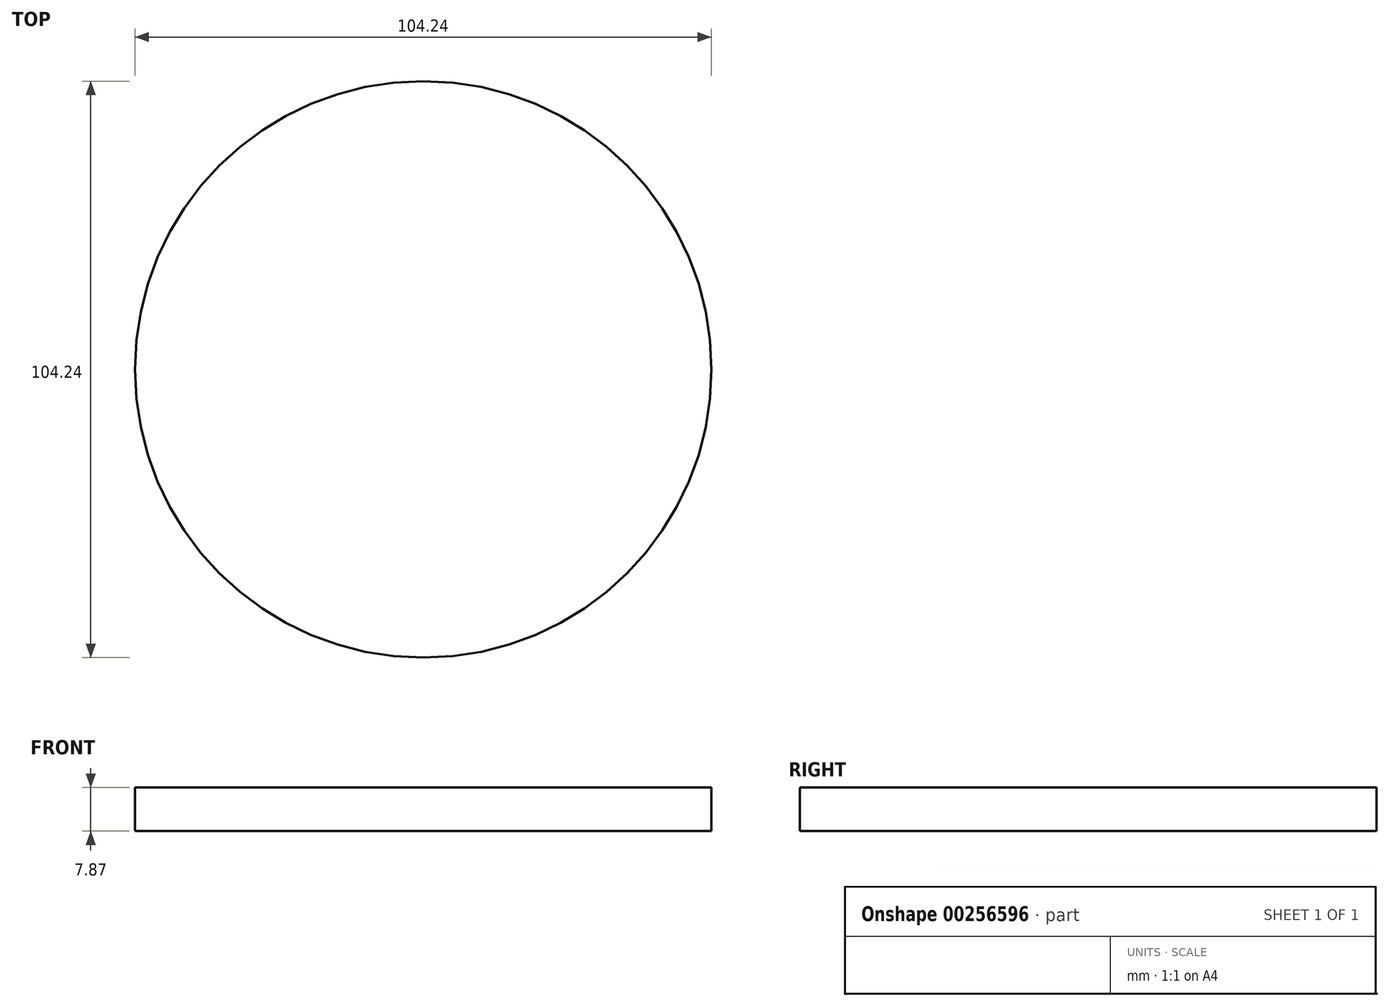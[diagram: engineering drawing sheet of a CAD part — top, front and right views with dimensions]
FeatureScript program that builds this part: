
annotation { "Feature Type Name" : "Feature", "Feature Type Description" : "" }
export const myFeature = defineFeature(function(context is Context, id is Id, definition is map)
    precondition{}
    {
        {
            var Q0;
            Q0=qCreatedBy(makeId("Top.planeOp"),FACE);
            var sketch = newSketch(context, id + "F0", { "sketchPlane" : qUnion([Q0])});
            skCircle(sketch, "E0", {"center": v(0, 0) * mm, "radius": 52.12 * mm});
            skSolve(sketch);
        }
        {
            var Q0;
            Q0 = qSketchRegion(id + "F0", true);
            extrude(context, id + "F1", {"entities" : qUnion([Q0]), "depth" : 7.87 * mm});
        }
    });
